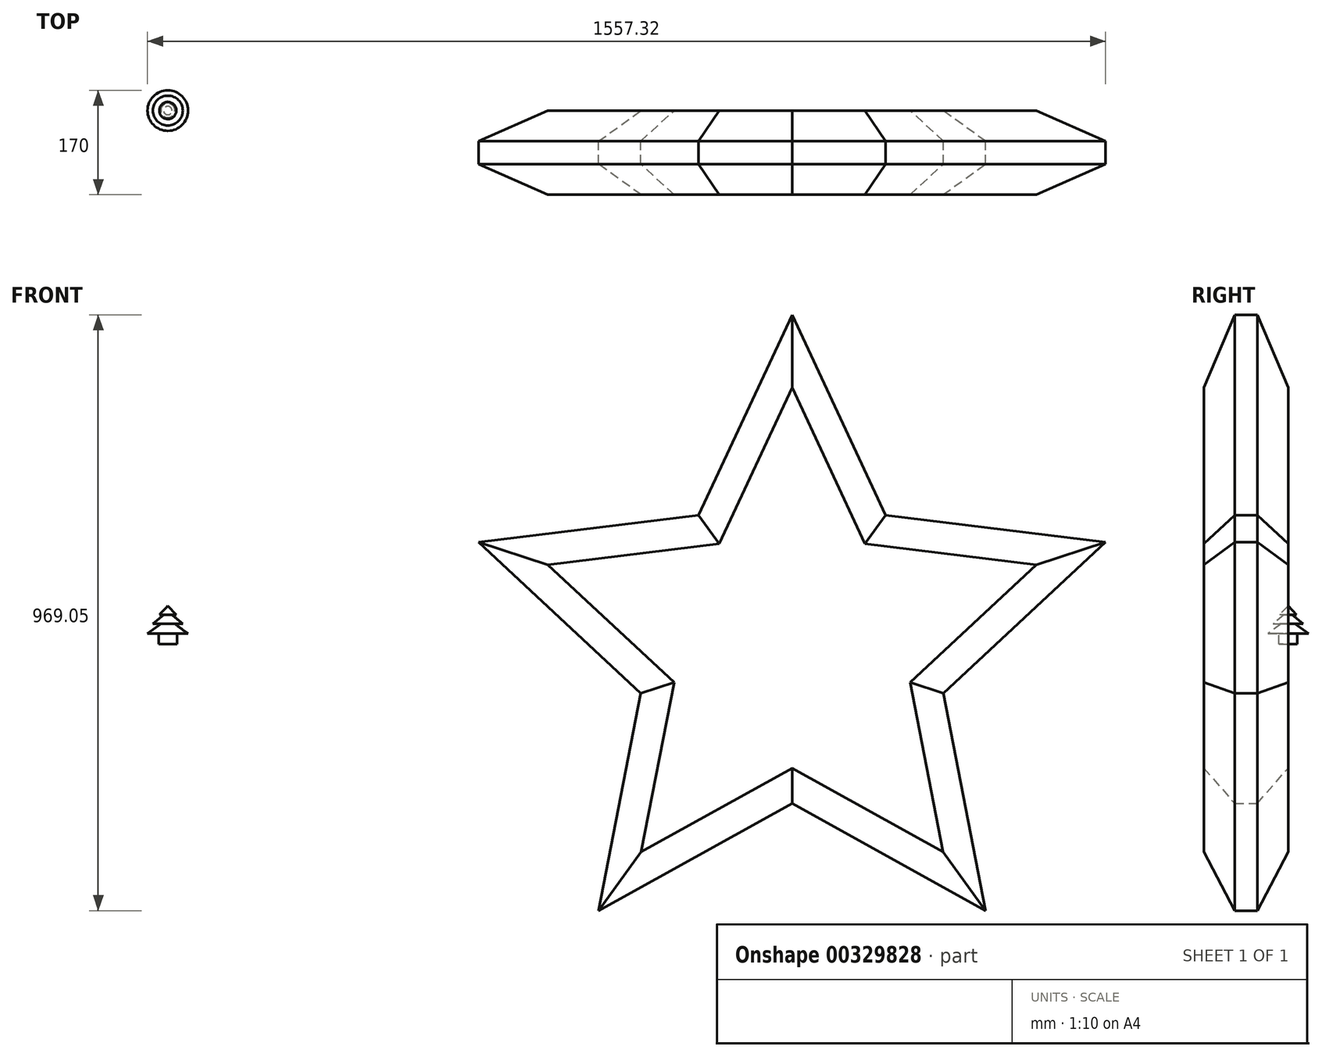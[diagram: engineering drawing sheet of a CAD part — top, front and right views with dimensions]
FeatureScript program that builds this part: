
annotation { "Feature Type Name" : "Feature", "Feature Type Description" : "" }
export const myFeature = defineFeature(function(context is Context, id is Id, definition is map)
    precondition{}
    {
        {
            var Q0;
            Q0=qCreatedBy(makeId("Front.planeOp"),FACE);
            var sketch = newSketch(context, id + "F0", { "sketchPlane" : qUnion([Q0])});
            skLineSegment(sketch, "E0", {"start": v(0, 0) * mm, "end": v(-15, 0) * mm});
            skLineSegment(sketch, "E1", {"start": v(-15, 0) * mm, "end": v(-15, 17) * mm});
            skLineSegment(sketch, "E2", {"start": v(-15, 17) * mm, "end": v(-33, 17) * mm});
            skLineSegment(sketch, "E3", {"start": v(-33, 17) * mm, "end": v(-11.25, 33) * mm});
            skLineSegment(sketch, "E4", {"start": v(-11.25, 33) * mm, "end": v(-24.25, 33) * mm});
            skLineSegment(sketch, "E5", {"start": v(-24.25, 33) * mm, "end": v(-6.82, 48) * mm});
            skLineSegment(sketch, "E6", {"start": v(-6.82, 48) * mm, "end": v(-13.82, 48) * mm});
            skLineSegment(sketch, "E7", {"start": v(-13.82, 48) * mm, "end": v(0, 62.46) * mm});
            skLineSegment(sketch, "E8", {"start": v(0, 62.46) * mm, "end": v(0, 0) * mm});
            skSolve(sketch);
        }
        {
            var Q0;
            Q0 = qSketchRegion(id + "F0", true);
            var Q1;
            Q1=sQuery(id+"F0.wireOp",EDGE,"E8");
            revolve(context, id + "F1", {"entities" : qUnion([Q0]), "axis" : qUnion([Q1]), "revolveType" : RevolveType.FULL});
        }
        {
            var Q0;
            Q0=qCreatedBy(makeId("Front.planeOp"),FACE);
            var sketch = newSketch(context, id + "F2", { "sketchPlane" : qUnion([Q0])});
            skLineSegment(sketch, "E9", {"start": v(1014.86, 535.68) * mm, "end": v(862.72, 209.4) * mm});
            skLineSegment(sketch, "E10", {"start": v(1014.86, 535.68) * mm, "end": v(1014.86, 209.4) * mm, "construction": true});
            skLineSegment(sketch, "E11.MirrorCS", {"start": v(1014.86, 535.68) * mm, "end": v(1167, 209.4) * mm});
            skLineSegment(sketch, "E12.1.0", {"start": v(505.4, 165.53) * mm, "end": v(768.7, -79.99) * mm});
            skLineSegment(sketch, "E12.1.1", {"start": v(505.4, 165.53) * mm, "end": v(862.72, 209.4) * mm});
            skLineSegment(sketch, "E12.2.0", {"start": v(700, -433.37) * mm, "end": v(1014.86, -258.84) * mm});
            skLineSegment(sketch, "E12.2.1", {"start": v(700, -433.37) * mm, "end": v(768.7, -79.99) * mm});
            skLineSegment(sketch, "E12.3.0", {"start": v(1329.73, -433.37) * mm, "end": v(1261.03, -79.99) * mm});
            skLineSegment(sketch, "E12.3.1", {"start": v(1329.73, -433.37) * mm, "end": v(1014.86, -258.84) * mm});
            skLineSegment(sketch, "E12.4.0", {"start": v(1524.32, 165.53) * mm, "end": v(1167, 209.4) * mm});
            skLineSegment(sketch, "E12.4.1", {"start": v(1524.32, 165.53) * mm, "end": v(1261.03, -79.99) * mm});
            skPoint(sketch, "E12.center", {"position": v(1014.86, 0) * mm});
            skSolve(sketch);
        }
        {
            var Q0;
            Q0 = qSketchRegion(id + "F2", true);
            extrude(context, id + "F3", {"entities" : qUnion([Q0]), "depth" : 137 * mm});
        }
        {
            var Q0;
            Q0=makeQuery(id+"F3.opExtrude","CAP_EDGE",EDGE,{"disambiguationData":[OSD([sQuery(id+"F2.wireOp",EDGE,"E12.1.1")])],"isStart":false});
            var Q1;
            Q1=makeQuery(id+"F3.opExtrude","CAP_EDGE",EDGE,{"disambiguationData":[OSD([sQuery(id+"F2.wireOp",EDGE,"E12.1.1")])],"isStart":true});
            var Q2;
            Q2=makeQuery(id+"F3.opExtrude","CAP_EDGE",EDGE,{"disambiguationData":[OSD([sQuery(id+"F2.wireOp",EDGE,"E9")])],"isStart":false});
            var Q3;
            Q3=makeQuery(id+"F3.opExtrude","CAP_EDGE",EDGE,{"disambiguationData":[OSD([sQuery(id+"F2.wireOp",EDGE,"E9")])],"isStart":true});
            var Q4;
            Q4=makeQuery(id+"F3.opExtrude","CAP_EDGE",EDGE,{"disambiguationData":[OSD([sQuery(id+"F2.wireOp",EDGE,"E12.4.0")])],"isStart":false});
            var Q5;
            Q5=makeQuery(id+"F3.opExtrude","CAP_EDGE",EDGE,{"disambiguationData":[OSD([sQuery(id+"F2.wireOp",EDGE,"E12.4.0")])],"isStart":true});
            var Q6;
            Q6=makeQuery(id+"F3.opExtrude","CAP_EDGE",EDGE,{"disambiguationData":[OSD([sQuery(id+"F2.wireOp",EDGE,"E12.2.1")])],"isStart":false});
            var Q7;
            Q7=makeQuery(id+"F3.opExtrude","CAP_EDGE",EDGE,{"disambiguationData":[OSD([sQuery(id+"F2.wireOp",EDGE,"E12.2.1")])],"isStart":true});
            var Q8;
            Q8=makeQuery(id+"F3.opExtrude","CAP_EDGE",EDGE,{"disambiguationData":[OSD([sQuery(id+"F2.wireOp",EDGE,"E12.1.0")])],"isStart":false});
            var Q9;
            Q9=makeQuery(id+"F3.opExtrude","CAP_EDGE",EDGE,{"disambiguationData":[OSD([sQuery(id+"F2.wireOp",EDGE,"E12.1.0")])],"isStart":true});
            var Q10;
            Q10=makeQuery(id+"F3.opExtrude","CAP_EDGE",EDGE,{"disambiguationData":[OSD([sQuery(id+"F2.wireOp",EDGE,"E12.2.0")])],"isStart":false});
            var Q11;
            Q11=makeQuery(id+"F3.opExtrude","CAP_EDGE",EDGE,{"disambiguationData":[OSD([sQuery(id+"F2.wireOp",EDGE,"E12.3.1")])],"isStart":false});
            var Q12;
            Q12=makeQuery(id+"F3.opExtrude","CAP_EDGE",EDGE,{"disambiguationData":[OSD([sQuery(id+"F2.wireOp",EDGE,"E12.3.0")])],"isStart":false});
            var Q13;
            Q13=makeQuery(id+"F3.opExtrude","CAP_EDGE",EDGE,{"disambiguationData":[OSD([sQuery(id+"F2.wireOp",EDGE,"E12.4.1")])],"isStart":false});
            var Q14;
            Q14=makeQuery(id+"F3.opExtrude","CAP_EDGE",EDGE,{"disambiguationData":[OSD([sQuery(id+"F2.wireOp",EDGE,"E11.MirrorCS")])],"isStart":false});
            var Q15;
            Q15=makeQuery(id+"F3.opExtrude","CAP_EDGE",EDGE,{"disambiguationData":[OSD([sQuery(id+"F2.wireOp",EDGE,"E11.MirrorCS")])],"isStart":true});
            var Q16;
            Q16=makeQuery(id+"F3.opExtrude","CAP_EDGE",EDGE,{"disambiguationData":[OSD([sQuery(id+"F2.wireOp",EDGE,"E12.4.1")])],"isStart":true});
            var Q17;
            Q17=makeQuery(id+"F3.opExtrude","CAP_EDGE",EDGE,{"disambiguationData":[OSD([sQuery(id+"F2.wireOp",EDGE,"E12.3.0")])],"isStart":true});
            var Q18;
            Q18=makeQuery(id+"F3.opExtrude","CAP_EDGE",EDGE,{"disambiguationData":[OSD([sQuery(id+"F2.wireOp",EDGE,"E12.2.0")])],"isStart":true});
            var Q19;
            Q19=makeQuery(id+"F3.opExtrude","CAP_EDGE",EDGE,{"disambiguationData":[OSD([sQuery(id+"F2.wireOp",EDGE,"E12.3.1")])],"isStart":true});
            chamfer(context, id + "F4", {"entities" : qUnion([Q0, Q1, Q2, Q3, Q4, Q5, Q6, Q7, Q8, Q9, Q10, Q11, Q12, Q13, Q14, Q15, Q16, Q17, Q18, Q19]), "width" : 50 * mm, "tangentPropagation" : true});
        }
    });
